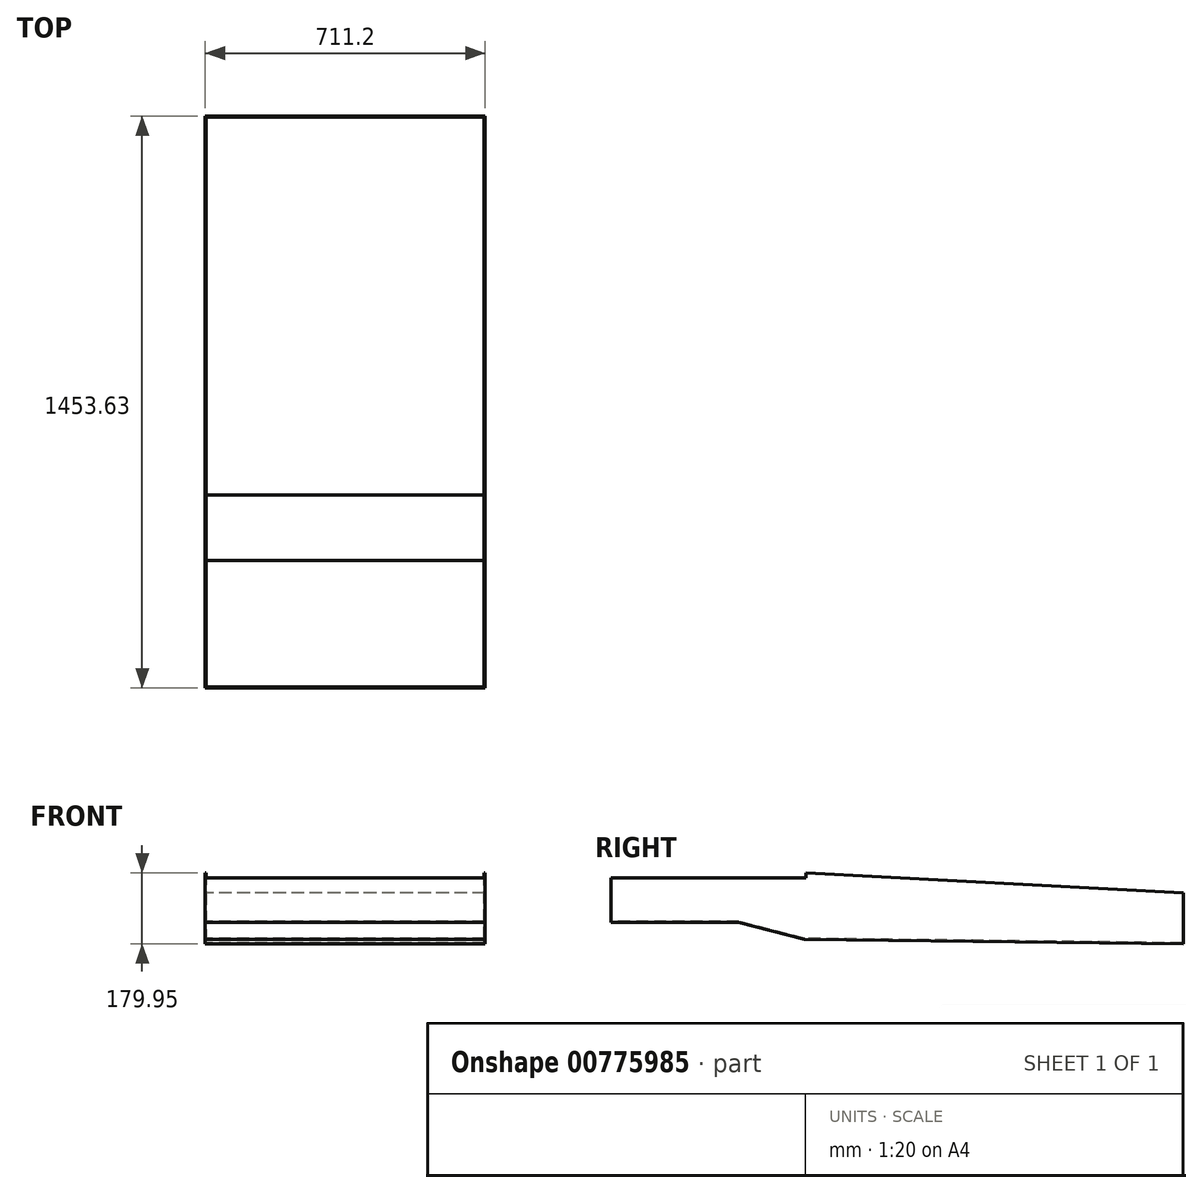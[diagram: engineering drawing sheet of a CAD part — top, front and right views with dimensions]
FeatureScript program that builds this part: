
annotation { "Feature Type Name" : "Feature", "Feature Type Description" : "" }
export const myFeature = defineFeature(function(context is Context, id is Id, definition is map)
    precondition{}
    {
        {
            var Q0;
            Q0=qCreatedBy(makeId("Right.planeOp"),FACE);
            var sketch = newSketch(context, id + "F0", { "sketchPlane" : qUnion([Q0])});
            skLineSegment(sketch, "E0", {"start": v(-6379.06, 259.72) * mm, "end": v(-6379.06, 130.48) * mm});
            skLineSegment(sketch, "E1", {"start": v(-6379.06, 130.48) * mm, "end": v(-7341.88, 141.86) * mm});
            skLineSegment(sketch, "E2", {"start": v(-7341.88, 141.86) * mm, "end": v(-7509.2, 185.24) * mm});
            skLineSegment(sketch, "E3", {"start": v(-7509.2, 185.24) * mm, "end": v(-7832.7, 185.24) * mm});
            skLineSegment(sketch, "E4", {"start": v(-7832.7, 185.24) * mm, "end": v(-7832.7, 298.03) * mm});
            skLineSegment(sketch, "E5", {"start": v(-7832.7, 298.03) * mm, "end": v(-7338.16, 298.03) * mm});
            skLineSegment(sketch, "E6", {"start": v(-7338.16, 298.03) * mm, "end": v(-7338.16, 310.43) * mm});
            skLineSegment(sketch, "E7", {"start": v(-7338.16, 310.43) * mm, "end": v(-6379.06, 259.72) * mm});
            skSolve(sketch);
        }
        {
            var Q0;
            Q0 = qSketchRegion(id + "F0", true);
            extrude(context, id + "F1", {"entities" : qUnion([Q0]), "depth" : 711.2 * mm, "offsetDistance" : 25.4 * mm, "symmetric" : true});
        }
        {
            var Q0;
            Q0=makeQuery(id+"F1.opExtrude","SWEPT_FACE",FACE,{"disambiguationData":[OSD([sQuery(id+"F0.wireOp",EDGE,"E7")])]});
            var Q1;
            Q1=makeQuery(id+"F1.opExtrude","SWEPT_FACE",FACE,{"disambiguationData":[OSD([sQuery(id+"F0.wireOp",EDGE,"E6")])]});
            var Q2;
            Q2=makeQuery(id+"F1.opExtrude","SWEPT_FACE",FACE,{"disambiguationData":[OSD([sQuery(id+"F0.wireOp",EDGE,"E5")])]});
            shell(context, id + "F2", {"entities" : qUnion([Q0, Q1, Q2]), "thickness" : 2.54 * mm});
        }
    });
